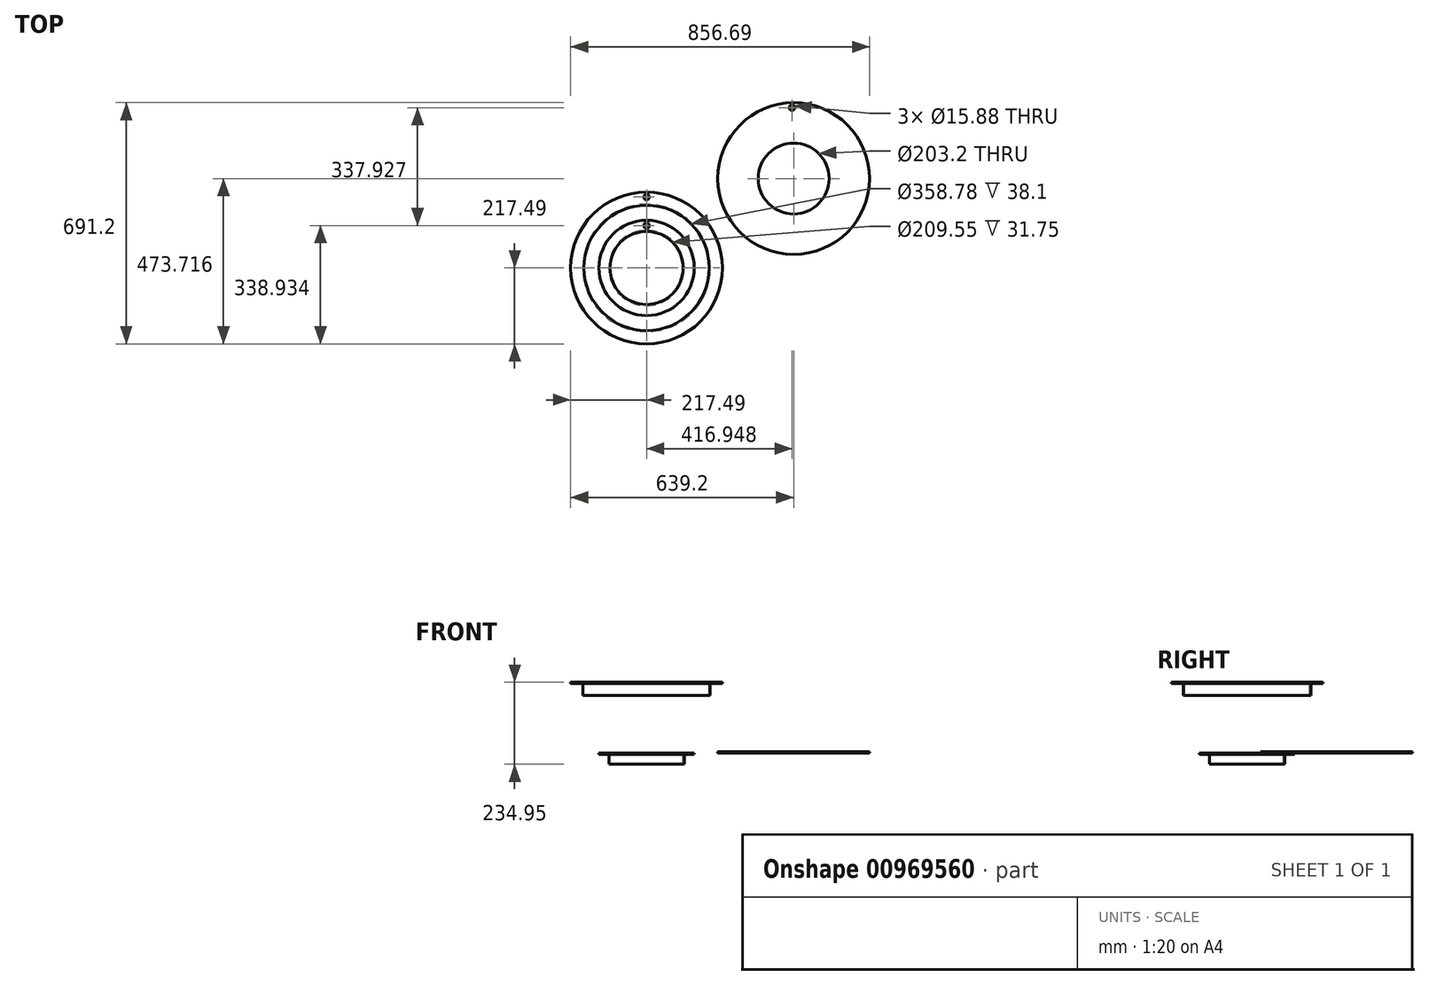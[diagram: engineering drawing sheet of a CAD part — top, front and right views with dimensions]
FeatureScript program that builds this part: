
annotation { "Feature Type Name" : "Feature", "Feature Type Description" : "" }
export const myFeature = defineFeature(function(context is Context, id is Id, definition is map)
    precondition{}
    {
        {
            var Q0;
            Q0=qCreatedBy(makeId("Front.planeOp"),FACE);
            var sketch = newSketch(context, id + "F0", { "sketchPlane" : qUnion([Q0])});
            skLineSegment(sketch, "E0", {"start": v(0, 56.07) * mm, "end": v(0, 14.45) * mm, "construction": true});
            skLineSegment(sketch, "E1", {"start": v(104.78, 0) * mm, "end": v(136.53, 0) * mm});
            skLineSegment(sketch, "E2", {"start": v(136.53, 0) * mm, "end": v(136.53, -3.18) * mm});
            skLineSegment(sketch, "E3", {"start": v(136.53, -3.18) * mm, "end": v(107.95, -3.18) * mm});
            skLineSegment(sketch, "E4", {"start": v(107.95, -3.18) * mm, "end": v(107.95, -31.75) * mm});
            skLineSegment(sketch, "E5", {"start": v(107.95, -31.75) * mm, "end": v(104.78, -31.75) * mm});
            skLineSegment(sketch, "E6", {"start": v(104.78, -31.75) * mm, "end": v(104.78, 0) * mm});
            skSolve(sketch);
        }
        {
            var Q0;
            Q0 = qSketchRegion(id + "F0", true);
            var Q1;
            Q1=sQuery(id+"F0.wireOp",EDGE,"E0");
            revolve(context, id + "F1", {"surfaceOperationType" : NewSurfaceOperationType.NEW, "entities" : qUnion([Q0]), "axis" : qUnion([Q1]), "revolveType" : RevolveType.FULL});
        }
        {
            var Q0;
            Q0=makeQuery(id+"F1.opRevolve","SWEPT_FACE",FACE,{"disambiguationData":[OSD([sQuery(id+"F0.wireOp",EDGE,"E1")])]});
            var sketch = newSketch(context, id + "F2", { "sketchPlane" : qUnion([Q0])});
            skCircle(sketch, "E7", {"center": v(0, 121.44) * mm, "radius": 7.94 * mm});
            skCircle(sketch, "E8", {"center": v(0, 0) * mm, "radius": 121.44 * mm, "construction": true});
            skSolve(sketch);
        }
        {
            var Q0;
            Q0 = qSketchRegion(id + "F2", true);
            extrude(context, id + "F3", {"entities" : qUnion([Q0]), "operationType" : NewBodyOperationType.REMOVE, "oppositeDirection" : true, "depth" : 25.4 * mm, "offsetDistance" : 25.4 * mm});
        }
        {
            var Q0;
            Q0=qCreatedBy(makeId("Front.planeOp"),FACE);
            var sketch = newSketch(context, id + "F4", { "sketchPlane" : qUnion([Q0])});
            skLineSegment(sketch, "E9", {"start": v(179.39, 203.2) * mm, "end": v(217.49, 203.2) * mm});
            skLineSegment(sketch, "E10", {"start": v(217.49, 203.2) * mm, "end": v(217.49, 200.03) * mm});
            skLineSegment(sketch, "E11", {"start": v(217.49, 200.03) * mm, "end": v(182.56, 200.03) * mm});
            skLineSegment(sketch, "E12", {"start": v(182.56, 200.03) * mm, "end": v(182.56, 165.1) * mm});
            skLineSegment(sketch, "E13", {"start": v(182.56, 165.1) * mm, "end": v(179.39, 165.1) * mm});
            skLineSegment(sketch, "E14", {"start": v(179.39, 165.1) * mm, "end": v(179.39, 203.2) * mm});
            skSolve(sketch);
        }
        {
            var Q0;
            Q0 = qSketchRegion(id + "F4", true);
            var Q1;
            Q1=sQuery(id+"F0.wireOp",EDGE,"E0");
            revolve(context, id + "F5", {"surfaceOperationType" : NewSurfaceOperationType.NEW, "entities" : qUnion([Q0]), "axis" : qUnion([Q1]), "revolveType" : RevolveType.FULL});
        }
        {
            var Q0;
            Q0=makeQuery(id+"F5.opRevolve","SWEPT_FACE",FACE,{"disambiguationData":[OSD([sQuery(id+"F4.wireOp",EDGE,"E9")])]});
            var sketch = newSketch(context, id + "F6", { "sketchPlane" : qUnion([Q0])});
            skCircle(sketch, "E15", {"center": v(0, 0) * mm, "radius": 203.2 * mm, "construction": true});
            skCircle(sketch, "E16", {"center": v(0, 203.2) * mm, "radius": 7.94 * mm});
            skSolve(sketch);
        }
        {
            var Q0;
            Q0 = qSketchRegion(id + "F6", true);
            extrude(context, id + "F7", {"entities" : qUnion([Q0]), "operationType" : NewBodyOperationType.REMOVE, "oppositeDirection" : true, "depth" : 25.4 * mm, "offsetDistance" : 25.4 * mm});
        }
        {
            var Q0;
            Q0=qCreatedBy(makeId("Top.planeOp"),FACE);
            var sketch = newSketch(context, id + "F8", { "sketchPlane" : qUnion([Q0])});
            skCircle(sketch, "E17", {"center": v(421.71, 256.23) * mm, "radius": 217.49 * mm});
            skSolve(sketch);
        }
        {
            var Q0;
            Q0 = qSketchRegion(id + "F8", true);
            extrude(context, id + "F9", {"entities" : qUnion([Q0]), "depth" : 4.76 * mm, "offsetDistance" : 25.4 * mm});
        }
        {
            var Q0;
            Q0=makeQuery(id+"F9.opExtrude","CAP_FACE",FACE,{"disambiguationData":[OSD([sQuery(id+"F8.wireOp",EDGE,"E17")])],"isStart":false});
            var sketch = newSketch(context, id + "F10", { "sketchPlane" : qUnion([Q0])});
            skCircle(sketch, "E18", {"center": v(416.95, 459.37) * mm, "radius": 7.94 * mm});
            skCircle(sketch, "E19", {"center": v(421.71, 256.23) * mm, "radius": 203.2 * mm, "construction": true});
            skSolve(sketch);
        }
        {
            var Q0;
            Q0 = qSketchRegion(id + "F10", true);
            extrude(context, id + "F11", {"entities" : qUnion([Q0]), "operationType" : NewBodyOperationType.REMOVE, "oppositeDirection" : true, "depth" : 25.4 * mm, "offsetDistance" : 25.4 * mm});
        }
        {
            var Q0;
            Q0=makeQuery(id+"F9.opExtrude","CAP_FACE",FACE,{"disambiguationData":[OSD([sQuery(id+"F8.wireOp",EDGE,"E17")])],"isStart":false});
            var sketch = newSketch(context, id + "F12", { "sketchPlane" : qUnion([Q0])});
            skCircle(sketch, "E20", {"center": v(421.71, 256.23) * mm, "radius": 101.6 * mm});
            skSolve(sketch);
        }
        {
            var Q0;
            Q0 = qSketchRegion(id + "F12", true);
            extrude(context, id + "F13", {"entities" : qUnion([Q0]), "operationType" : NewBodyOperationType.REMOVE, "oppositeDirection" : true, "depth" : 25.4 * mm, "offsetDistance" : 25.4 * mm});
        }
    });
